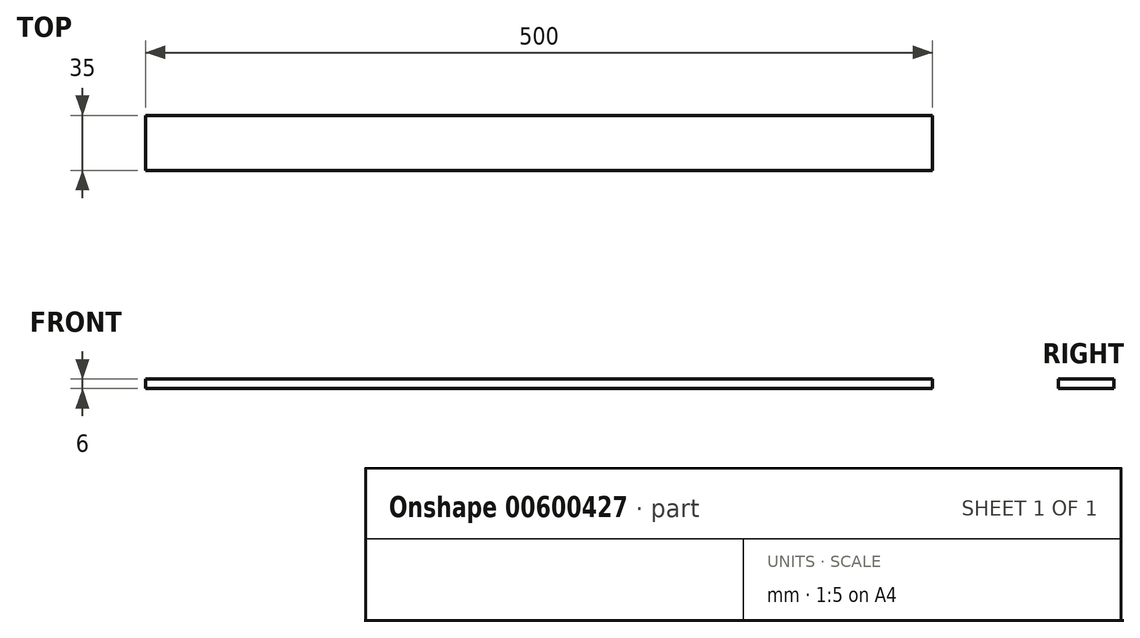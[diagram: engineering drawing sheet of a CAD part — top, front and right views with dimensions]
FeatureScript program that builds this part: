
annotation { "Feature Type Name" : "Feature", "Feature Type Description" : "" }
export const myFeature = defineFeature(function(context is Context, id is Id, definition is map)
    precondition{}
    {
        {
            var Q0;
            Q0=qCreatedBy(makeId("Top.planeOp"),FACE);
            var sketch = newSketch(context, id + "F0", { "sketchPlane" : qUnion([Q0])});
            skLineSegment(sketch, "E0.bottom", {"start": v(-344.09, -97.58) * mm, "end": v(155.91, -97.58) * mm});
            skLineSegment(sketch, "E0.top", {"start": v(-344.09, -132.58) * mm, "end": v(155.91, -132.58) * mm});
            skLineSegment(sketch, "E0.left", {"start": v(-344.09, -97.58) * mm, "end": v(-344.09, -132.58) * mm});
            skLineSegment(sketch, "E0.right", {"start": v(155.91, -97.58) * mm, "end": v(155.91, -132.58) * mm});
            skSolve(sketch);
        }
        {
            var Q0;
            Q0 = qSketchRegion(id + "F0", true);
            extrude(context, id + "F1", {"entities" : qUnion([Q0]), "depth" : 6 * mm, "offsetDistance" : 25 * mm});
        }
    });
